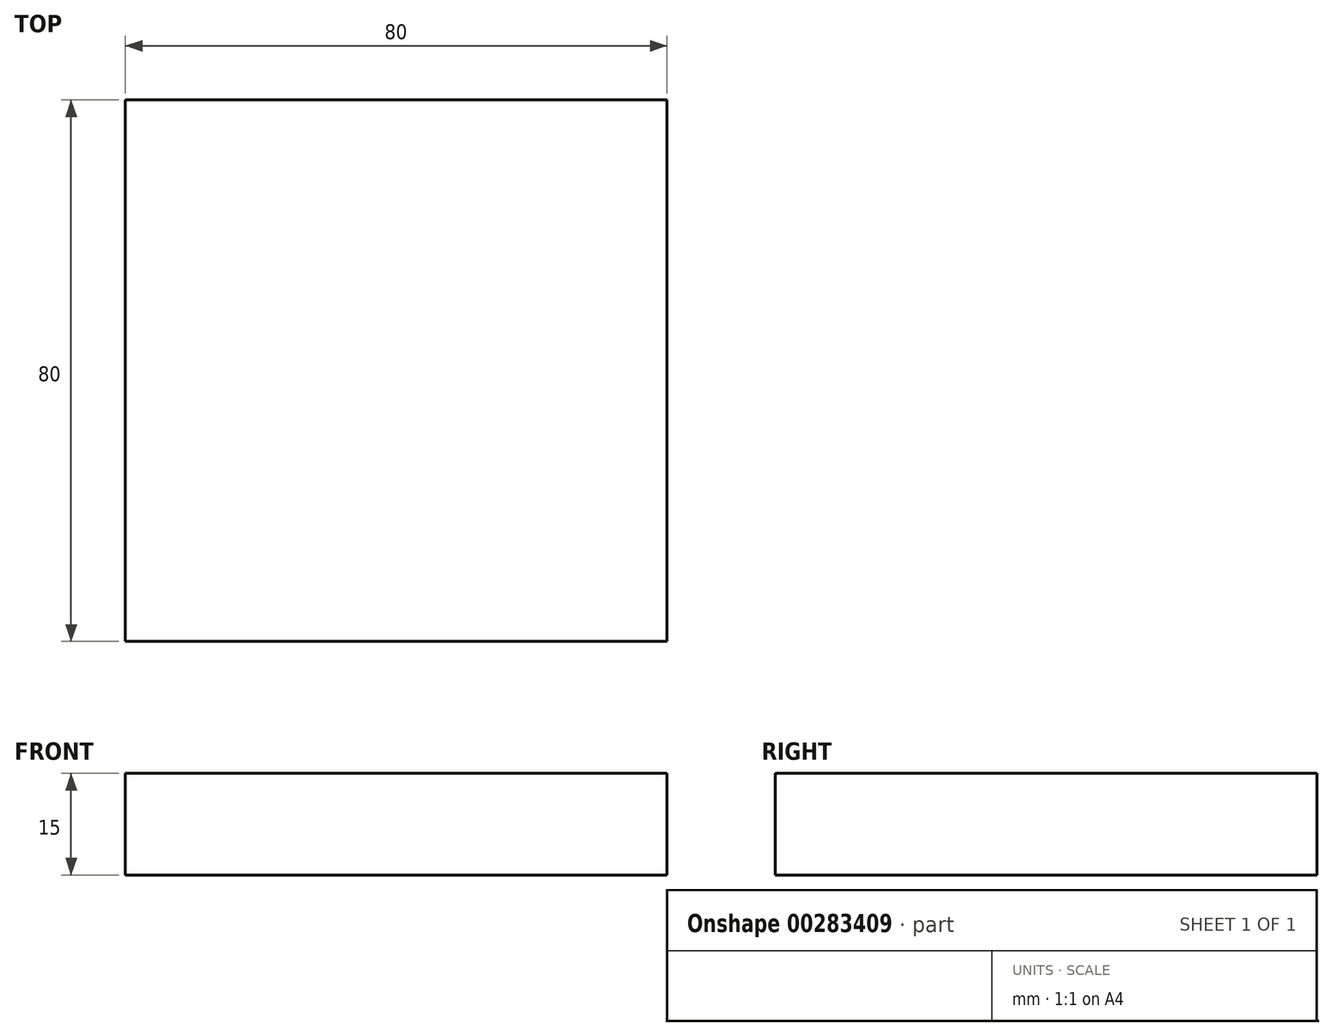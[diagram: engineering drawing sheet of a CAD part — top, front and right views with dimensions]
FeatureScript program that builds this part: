
annotation { "Feature Type Name" : "Feature", "Feature Type Description" : "" }
export const myFeature = defineFeature(function(context is Context, id is Id, definition is map)
    precondition{}
    {
        {
            var Q0;
            Q0=qCreatedBy(makeId("Top.planeOp"),FACE);
            var sketch = newSketch(context, id + "F0", { "sketchPlane" : qUnion([Q0])});
            skLineSegment(sketch, "E0.bottom", {"start": v(40, -40) * mm, "end": v(-40, -40) * mm});
            skLineSegment(sketch, "E0.top", {"start": v(40, 40) * mm, "end": v(-40, 40) * mm});
            skLineSegment(sketch, "E0.left", {"start": v(40, -40) * mm, "end": v(40, 40) * mm});
            skLineSegment(sketch, "E0.right", {"start": v(-40, -40) * mm, "end": v(-40, 40) * mm});
            skPoint(sketch, "E0.middle", {"position": v(0, 0) * mm});
            skSolve(sketch);
        }
        {
            var Q0;
            Q0 = qSketchRegion(id + "F0", true);
            extrude(context, id + "F1", {"entities" : qUnion([Q0]), "depth" : 15 * mm});
        }
    });
